# Revit family: Термостатический клапан HERZ-TS-99-FV с точной ступенчатой, открытой преднастройкой, угловой, осевой специальный 7528
name_source: partatom
category: Rohrzubehör
units: mm (PartAtom-declared; Revit-internal decimal feet)

## family parameters
Arbeitsebenenbasiert = Nein
Beim Laden mit Abzugskörper schneiden = Nein
Bemaßung runder Anschluss = Durchmesser verwenden
Gemeinsam genutzt = Nein
Immer vertikal = Ja
OmniClass-Nummer = 23.65.55.14
OmniClass-Titel = Valves for Liquid Services
Teiletyp = Unterbricht

## types (16) — shared parameters
Hersteller = HERZ Armaturen Ges.m.b.H.
L04 = 3.5 mm  [stored 0.0114829 ft]
LO1 = 16 mm  [stored 0.0524934 ft]
R05 = 4 mm  [stored 0.0131234 ft]
S01 = 10 mm  [stored 0.0328084 ft]
SCRNCODE = 05;00;02
SCRNSEQ = ARM;ARM_TYP="ALLF";2
URL = www.herz-armaturen.ru
Защитный колпачок = Пластик, пурпурный
Исполнение = Все модели поставляются в никелированном исполнении с пурпурным защитным колпачком.
Корпус = Никелированная латунь
Макс. рабочая температура = 120 °C
Макс. рабочее давление = 1000000.0 Pa
Область применения = Системы водяного отопления с большим перепадом температуры
Соединительная резьба для термостатической головки = M28x1.5
Среда = Качество воды в соответствии с ÖNORM H 5195 или директивой VDI 2035.

## per-type parameters (varying)
| type | TH_Kopf_7230 | TH_Kopf_7260 | TH_Kopf_9200_03 | TH_Kopf_9200_06 | TH_Kopf_9200_13 | TH_Kopf_9200_16 | TH_Kopf_9200_30 | TH_Kopf_9200_60 | TH_Kopf_9230 | TH_Kopf_9260 | TH_Kopf_9330_10000mm | TH_Kopf_9330_2000mm | TH_Kopf_9330_5000mm | TH_Kopf_9330_8000mm | TH_Kopf_9860 | Номер заказа термостатической головки |
| Без термостатической головки | Nein | Nein | Nein | Nein | Nein | Nein | Nein | Nein | Nein | Nein | Nein | Nein | Nein | Nein | Nein | 0 |
| С термостатической головкой_7230 | Ja | Nein | Nein | Nein | Nein | Nein | Nein | Nein | Nein | Nein | Nein | Nein | Nein | Nein | Nein | 1723006 |
| С термостатической головкой_7260 | Nein | Ja | Nein | Nein | Nein | Nein | Nein | Nein | Nein | Nein | Nein | Nein | Nein | Nein | Nein | 1726006 |
| С термостатической головкой_9200_03 | Nein | Nein | Ja | Nein | Nein | Nein | Nein | Nein | Nein | Nein | Nein | Nein | Nein | Nein | Nein | 1920003 |
| С термостатической головкой_9200_06 | Nein | Nein | Nein | Ja | Nein | Nein | Nein | Nein | Nein | Nein | Nein | Nein | Nein | Nein | Nein | 1920006 |
| С термостатической головкой_9200_13 | Nein | Nein | Nein | Nein | Ja | Nein | Nein | Nein | Nein | Nein | Nein | Nein | Nein | Nein | Nein | 1920013 |
| С термостатической головкой_9200_16 | Nein | Nein | Nein | Nein | Nein | Ja | Nein | Nein | Nein | Nein | Nein | Nein | Nein | Nein | Nein | 1920016 |
| С термостатической головкой_9200_30 | Nein | Nein | Nein | Nein | Nein | Nein | Ja | Nein | Nein | Nein | Nein | Nein | Nein | Nein | Nein | 1920030 |
| С термостатической головкой_9200_60 | Nein | Nein | Nein | Nein | Nein | Nein | Nein | Ja | Nein | Nein | Nein | Nein | Nein | Nein | Nein | 1920060 |
| С термостатической головкой_9230 | Nein | Nein | Nein | Nein | Nein | Nein | Nein | Nein | Ja | Nein | Nein | Nein | Nein | Nein | Nein | 1923006 |
| С термостатической головкой_9260 | Nein | Nein | Nein | Nein | Nein | Nein | Nein | Nein | Nein | Ja | Nein | Nein | Nein | Nein | Nein | 1926006 |
| С термостатической головкой_9330_10000мм | Nein | Nein | Nein | Nein | Nein | Nein | Nein | Nein | Nein | Nein | Ja | Nein | Nein | Nein | Nein | 1933020 |
| С термостатической головкой_9330_2000мм | Nein | Nein | Nein | Nein | Nein | Nein | Nein | Nein | Nein | Nein | Nein | Ja | Nein | Nein | Nein | 1933005 |
| С термостатической головкой_9330_5000мм | Nein | Nein | Nein | Nein | Nein | Nein | Nein | Nein | Nein | Nein | Nein | Nein | Ja | Nein | Nein | 1933010 |
| С термостатической головкой_9330_8000мм | Nein | Nein | Nein | Nein | Nein | Nein | Nein | Nein | Nein | Nein | Nein | Nein | Nein | Ja | Nein | 1933018 |
| С термостатической головкой_9860 | Nein | Nein | Nein | Nein | Nein | Nein | Nein | Nein | Nein | Nein | Nein | Nein | Nein | Nein | Ja | 1986010 |

note: [stored X ft] marks values corroborated as IEEE doubles in the binary element streams (Revit-internal decimal feet)
